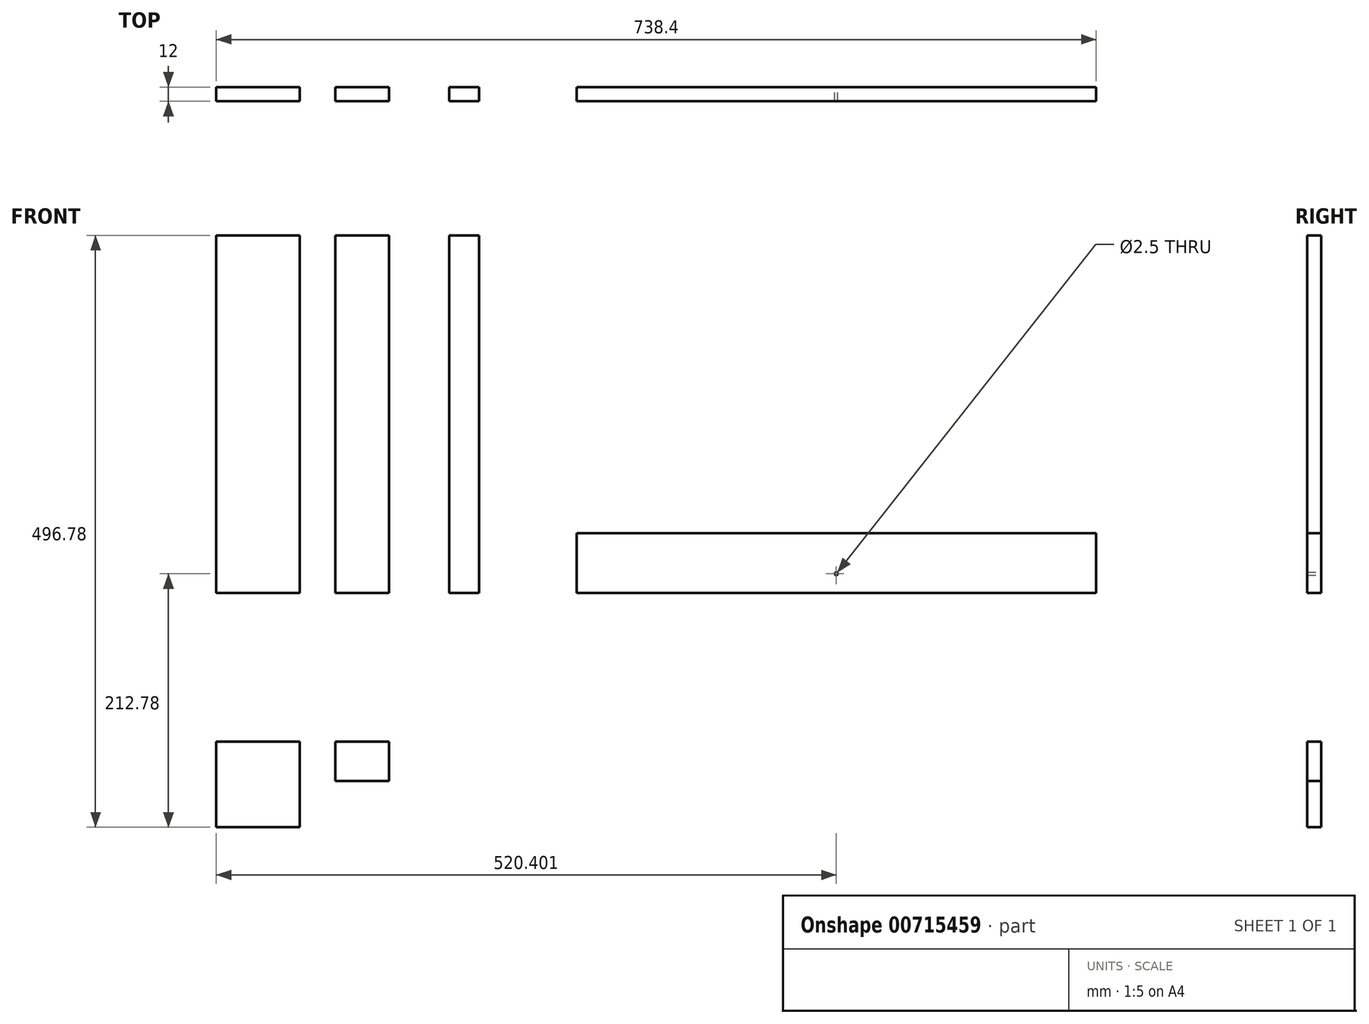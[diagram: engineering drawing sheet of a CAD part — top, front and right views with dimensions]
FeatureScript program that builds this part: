
annotation { "Feature Type Name" : "Feature", "Feature Type Description" : "" }
export const myFeature = defineFeature(function(context is Context, id is Id, definition is map)
    precondition{}
    {
        {
            var Q0;
            Q0=qCreatedBy(makeId("Front.planeOp"),FACE);
            var sketch = newSketch(context, id + "F0", { "sketchPlane" : qUnion([Q0])});
            skLineSegment(sketch, "E0.bottom", {"start": v(-70, 0) * mm, "end": v(0, 0) * mm});
            skLineSegment(sketch, "E0.top", {"start": v(-70, 300) * mm, "end": v(0, 300) * mm});
            skLineSegment(sketch, "E0.left", {"start": v(-70, 0) * mm, "end": v(-70, 300) * mm});
            skLineSegment(sketch, "E0.right", {"start": v(0, 0) * mm, "end": v(0, 300) * mm});
            skLineSegment(sketch, "E1.bottom", {"start": v(29.96, 0) * mm, "end": v(74.96, 0) * mm});
            skLineSegment(sketch, "E1.top", {"start": v(29.96, 300) * mm, "end": v(74.96, 300) * mm});
            skLineSegment(sketch, "E1.left", {"start": v(29.96, 0) * mm, "end": v(29.96, 300) * mm});
            skLineSegment(sketch, "E1.right", {"start": v(74.96, 0) * mm, "end": v(74.96, 300) * mm});
            skLineSegment(sketch, "E2.bottom", {"start": v(125.53, 0) * mm, "end": v(150.53, 0) * mm});
            skLineSegment(sketch, "E2.top", {"start": v(125.53, 300) * mm, "end": v(150.53, 300) * mm});
            skLineSegment(sketch, "E2.left", {"start": v(125.53, 0) * mm, "end": v(125.53, 300) * mm});
            skLineSegment(sketch, "E2.right", {"start": v(150.53, 0) * mm, "end": v(150.53, 300) * mm});
            skLineSegment(sketch, "E3.bottom", {"start": v(232.4, 0) * mm, "end": v(668.4, 0) * mm});
            skLineSegment(sketch, "E3.top", {"start": v(232.4, 50) * mm, "end": v(668.4, 50) * mm});
            skLineSegment(sketch, "E3.left", {"start": v(232.4, 0) * mm, "end": v(232.4, 50) * mm});
            skLineSegment(sketch, "E3.right", {"start": v(668.4, 0) * mm, "end": v(668.4, 50) * mm});
            skLineSegment(sketch, "E4.bottom", {"start": v(-70, -124.78) * mm, "end": v(0, -124.78) * mm});
            skLineSegment(sketch, "E4.top", {"start": v(-70, -196.78) * mm, "end": v(0, -196.78) * mm});
            skLineSegment(sketch, "E4.left", {"start": v(-70, -124.78) * mm, "end": v(-70, -196.78) * mm});
            skLineSegment(sketch, "E4.right", {"start": v(0, -124.78) * mm, "end": v(0, -196.78) * mm});
            skLineSegment(sketch, "E5.bottom", {"start": v(29.96, -124.78) * mm, "end": v(74.96, -124.78) * mm});
            skLineSegment(sketch, "E5.top", {"start": v(29.96, -157.78) * mm, "end": v(74.96, -157.78) * mm});
            skLineSegment(sketch, "E5.left", {"start": v(29.96, -124.78) * mm, "end": v(29.96, -157.78) * mm});
            skLineSegment(sketch, "E5.right", {"start": v(74.96, -124.78) * mm, "end": v(74.96, -157.78) * mm});
            skLineSegment(sketch, "E6", {"start": v(450.4, 0) * mm, "end": v(450.4, 50) * mm, "construction": true});
            skCircle(sketch, "E7", {"center": v(450.4, 16) * mm, "radius": 1.25 * mm});
            skCircle(sketch, "E8", {"center": v(450.4, 16) * mm, "radius": 16 * mm, "construction": true});
            skSolve(sketch);
        }
        {
            var Q0;
            Q0 = qSketchRegion(id + "F0", true);
            extrude(context, id + "F1", {"entities" : qUnion([Q0]), "depth" : 12 * mm, "offsetDistance" : 25 * mm});
        }
    });
